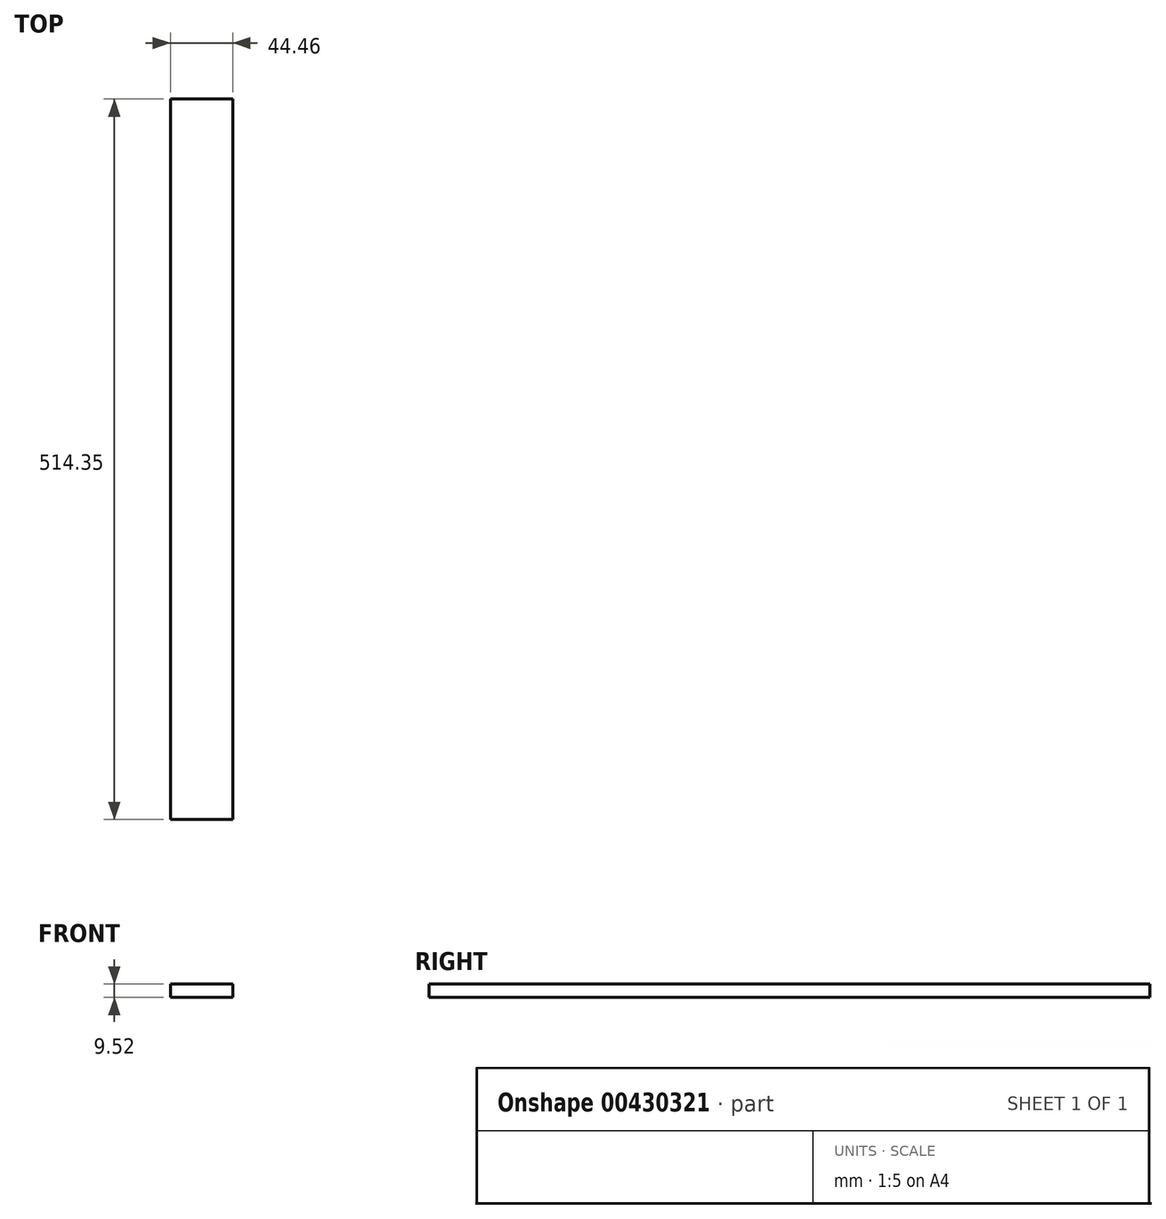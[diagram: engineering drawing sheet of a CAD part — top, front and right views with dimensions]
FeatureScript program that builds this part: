
annotation { "Feature Type Name" : "Feature", "Feature Type Description" : "" }
export const myFeature = defineFeature(function(context is Context, id is Id, definition is map)
    precondition{}
    {
        {
            var Q0;
            Q0=qCreatedBy(makeId("Front.planeOp"),FACE);
            var sketch = newSketch(context, id + "F0", { "sketchPlane" : qUnion([Q0])});
            skLineSegment(sketch, "E0.bottom", {"start": v(22.22, 4.76) * mm, "end": v(-22.23, 4.76) * mm});
            skLineSegment(sketch, "E0.top", {"start": v(22.22, -4.76) * mm, "end": v(-22.23, -4.76) * mm});
            skLineSegment(sketch, "E0.left", {"start": v(22.23, 4.76) * mm, "end": v(22.23, -4.76) * mm});
            skLineSegment(sketch, "E0.right", {"start": v(-22.23, 4.76) * mm, "end": v(-22.23, -4.76) * mm});
            skPoint(sketch, "E0.middle", {"position": v(0, 0) * mm});
            skSolve(sketch);
        }
        {
            var Q0;
            Q0=makeQuery(id+"F0.imprint","IMPRINT",FACE,{"disambiguationData":[TD([[makeQuery(id+"F0.imprint","IMPRINT",EDGE,{"derivedFrom":sQuery(id+"F0.wireOp",EDGE,"E0.bottom")}),1.0]])]});
            extrude(context, id + "F1", {"entities" : qUnion([Q0]), "depth" : 514.35 * mm});
        }
    });
